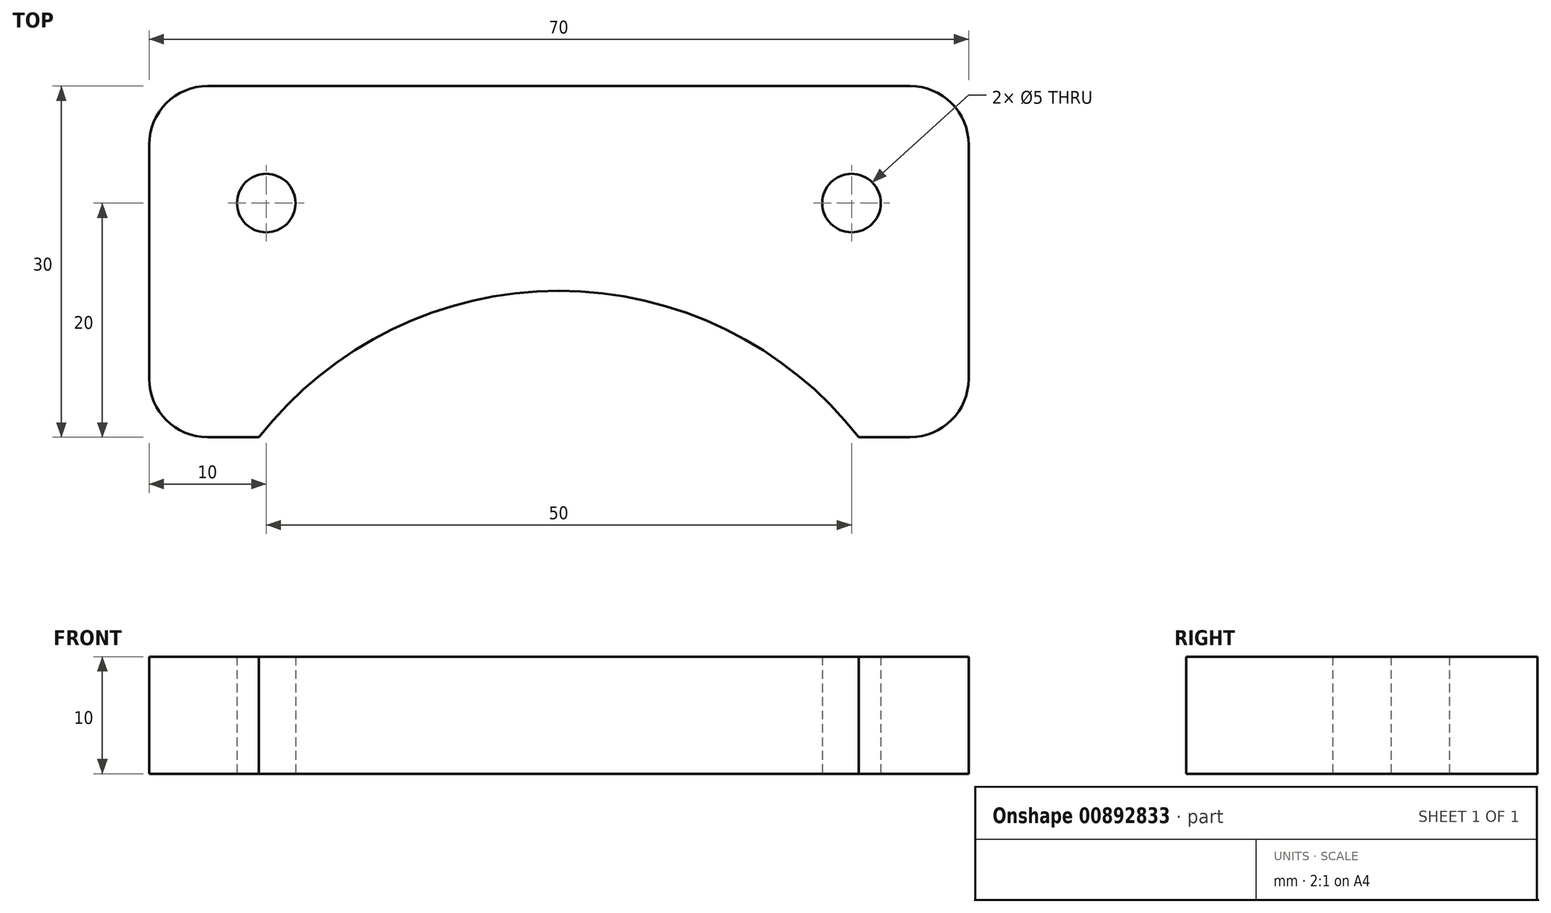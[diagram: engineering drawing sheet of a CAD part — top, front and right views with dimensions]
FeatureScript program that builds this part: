
annotation { "Feature Type Name" : "Feature", "Feature Type Description" : "" }
export const myFeature = defineFeature(function(context is Context, id is Id, definition is map)
    precondition{}
    {
        {
            var Q0;
            Q0=qCreatedBy(makeId("Top.planeOp"),FACE);
            var sketch = newSketch(context, id + "F0", { "sketchPlane" : qUnion([Q0])});
            skLineSegment(sketch, "E0.bottom", {"start": v(-30, 50) * mm, "end": v(30, 50) * mm});
            skLineSegment(sketch, "E0.left", {"start": v(-35, 45) * mm, "end": v(-35, 25) * mm});
            skLineSegment(sketch, "E0.right", {"start": v(35, 45) * mm, "end": v(35, 25) * mm});
            skLineSegment(sketch, "E1", {"start": v(0, 32.5) * mm, "end": v(0, 50) * mm, "construction": true});
            skLineSegment(sketch, "E2", {"start": v(-25, 50) * mm, "end": v(-25, 20) * mm, "construction": true});
            skLineSegment(sketch, "E3", {"start": v(-35, 40) * mm, "end": v(35, 40) * mm, "construction": true});
            skLineSegment(sketch, "E4.MirrorCS", {"start": v(25, 50) * mm, "end": v(25, 20) * mm, "construction": true});
            skCircle(sketch, "E5", {"center": v(-25, 40) * mm, "radius": 2.5 * mm});
            skCircle(sketch, "E6", {"center": v(25, 40) * mm, "radius": 2.5 * mm});
            skArc(sketch, "E7", {"start": v(25.62, 20) * mm, "mid": v(0, 32.5) * mm, "end": v(-25.62, 20) * mm});
            skLineSegment(sketch, "E8", {"start": v(-35, 20) * mm, "end": v(-25.62, 20) * mm});
            skLineSegment(sketch, "E9.trimOffspring", {"start": v(25.62, 20) * mm, "end": v(35, 20) * mm});
            skLineSegment(sketch, "E10", {"start": v(0, 50) * mm, "end": v(0, 0) * mm, "construction": true});
            skLineSegment(sketch, "E11", {"start": v(-30, 20) * mm, "end": v(30, 20) * mm, "construction": true});
            skPoint(sketch, "E12.visualSharp", {"position": v(-35, 50) * mm});
            skArc(sketch, "E12.filletArc", {"start": v(-30, 50) * mm, "mid": v(-33.54, 48.54) * mm, "end": v(-35, 45) * mm});
            skPoint(sketch, "E13.visualSharp", {"position": v(-35, 20) * mm});
            skArc(sketch, "E13.filletArc", {"start": v(-35, 25) * mm, "mid": v(-33.54, 21.46) * mm, "end": v(-30, 20) * mm});
            skPoint(sketch, "E14.visualSharp", {"position": v(35, 50) * mm});
            skArc(sketch, "E14.filletArc", {"start": v(35, 45) * mm, "mid": v(33.54, 48.54) * mm, "end": v(30, 50) * mm});
            skPoint(sketch, "E15.visualSharp", {"position": v(35, 20) * mm});
            skArc(sketch, "E15.filletArc", {"start": v(30, 20) * mm, "mid": v(33.54, 21.46) * mm, "end": v(35, 25) * mm});
            skSolve(sketch);
        }
        {
            var Q0;
            {var subQ1=sQuery(id+"F0.wireOp",EDGE,"E0.bottom");Q0=makeQuery(id+"F0.imprint","IMPRINT",FACE,{"disambiguationData":[TD([[makeQuery(id+"F0.imprint","IMPRINT",EDGE,{"derivedFrom":subQ1}),-1.0]])]});}
            extrude(context, id + "F1", {"entities" : qUnion([Q0]), "depth" : 10 * mm, "offsetDistance" : 25 * mm});
        }
    });
